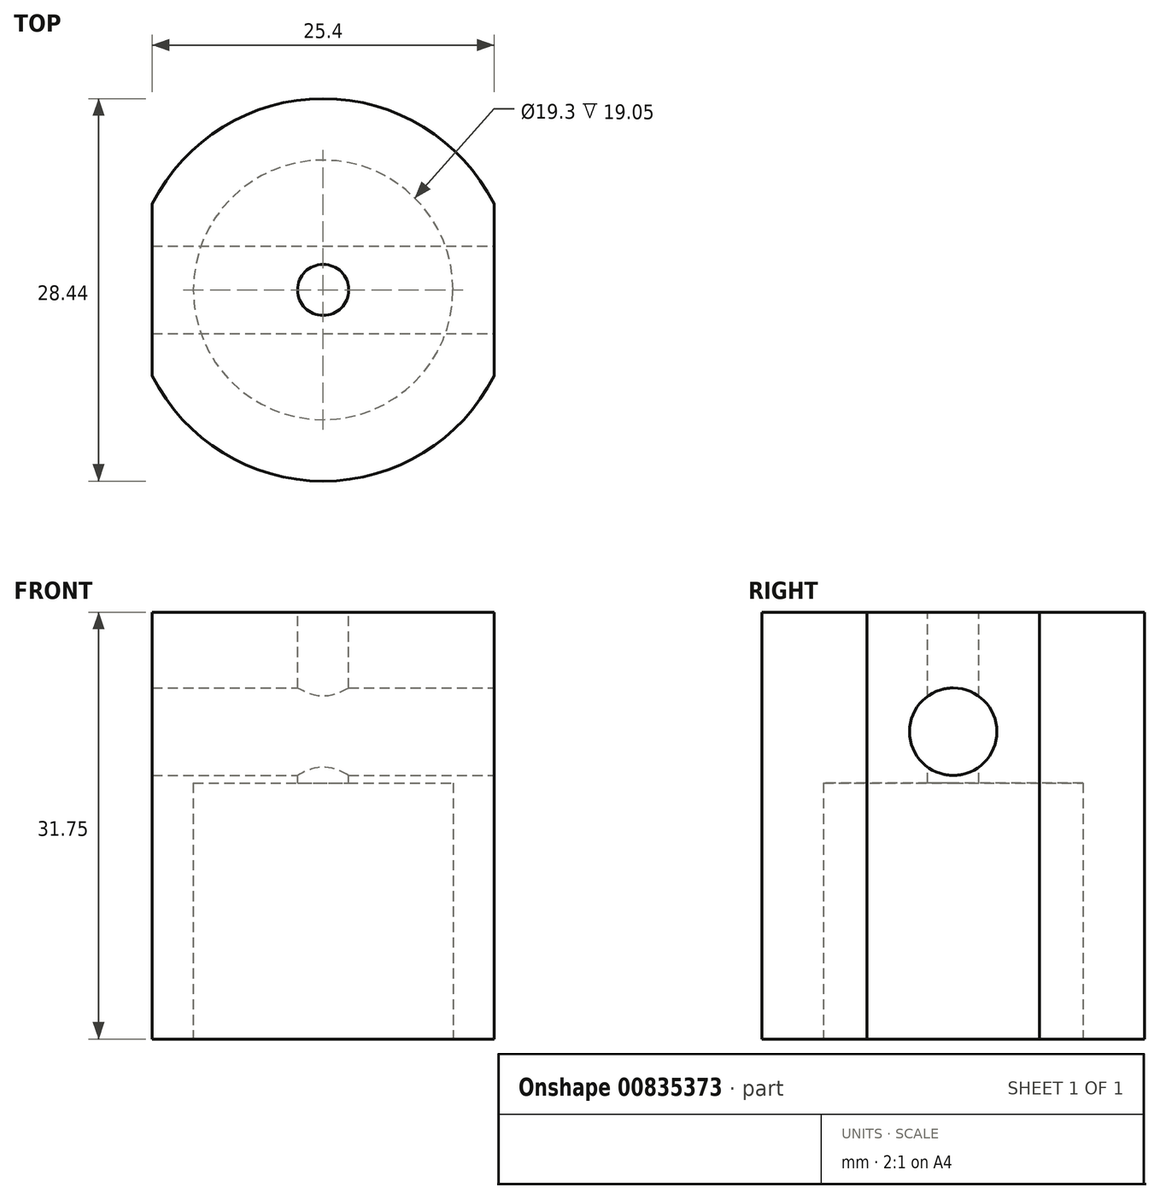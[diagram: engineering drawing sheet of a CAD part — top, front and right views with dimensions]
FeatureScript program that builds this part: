
annotation { "Feature Type Name" : "Feature", "Feature Type Description" : "" }
export const myFeature = defineFeature(function(context is Context, id is Id, definition is map)
    precondition{}
    {
        {
            var Q0;
            Q0=qCreatedBy(makeId("Top.planeOp"),FACE);
            var sketch = newSketch(context, id + "F0", { "sketchPlane" : qUnion([Q0])});
            skCircle(sketch, "E0", {"center": v(0, 0) * mm, "radius": 14.22 * mm});
            skSolve(sketch);
        }
        {
            var Q0;
            Q0 = qSketchRegion(id + "F0", true);
            extrude(context, id + "F1", {"entities" : qUnion([Q0]), "depth" : 31.75 * mm, "offsetDistance" : 25.4 * mm});
        }
        {
            var Q0;
            Q0=makeQuery(id+"F1.opExtrude","CAP_FACE",FACE,{"disambiguationData":[OSD([sQuery(id+"F0.wireOp",EDGE,"E0")])],"isStart":true});
            var sketch = newSketch(context, id + "F2", { "sketchPlane" : qUnion([Q0])});
            skCircle(sketch, "E1", {"center": v(0, 0) * mm, "radius": 9.65 * mm});
            skSolve(sketch);
        }
        {
            var Q0;
            Q0 = qSketchRegion(id + "F2", true);
            extrude(context, id + "F3", {"entities" : qUnion([Q0]), "operationType" : NewBodyOperationType.REMOVE, "oppositeDirection" : true, "depth" : 19.05 * mm, "offsetDistance" : 25.4 * mm});
        }
        {
            var Q0;
            Q0=makeQuery(id+"F1.opExtrude","CAP_FACE",FACE,{"disambiguationData":[OSD([sQuery(id+"F0.wireOp",EDGE,"E0")])],"isStart":false});
            var sketch = newSketch(context, id + "F4", { "sketchPlane" : qUnion([Q0])});
            skPoint(sketch, "E2", {"position": v(0, 0) * mm});
            skSolve(sketch);
        }
        {
            var Q0;
            Q0=sQuery(id+"F4.wireOp",VERTEX,"E2");
            var Q1;
            Q1=makeQuery(id+"F1.opExtrude","SWEPT_BODY",BODY,{"disambiguationData":[OSD([sQuery(id+"F0.wireOp",EDGE,"E0")])]});
            hole(context, id + "F5", {"style" : HoleStyle.SIMPLE, "endStyle" : HoleEndStyle.THROUGH, "standardTappedOrClearance" : lookupTablePath({ "standard" : "ANSI", "engagement" : "75%", "pitch" : "24 tpi", "size" : "#10", "type" : "Tapped" }), "standardBlindInLast" : lookupTablePath({ "standard" : "ANSI", "engagement" : "75%", "pitch" : "24 tpi", "size" : "#10", "type" : "Tapped" }), "holeDiameter" : 3.8 * mm, "majorDiameter" : 4.83 * mm, "showTappedDepth" : true, "tappedDepth" : 6.36 * mm, "tapClearance" : 3, "locations" : qUnion([Q0]), "scope" : qUnion([Q1])});
        }
        {
            var Q0;
            Q0=makeQuery(id+"F1.opExtrude","CAP_FACE",FACE,{"disambiguationData":[OSD([sQuery(id+"F0.wireOp",EDGE,"E0")])],"isStart":false});
            var sketch = newSketch(context, id + "F6", { "sketchPlane" : qUnion([Q0])});
            skArc(sketch, "E3.0", {"start": v(-12.7, 6.4) * mm, "mid": v(-14.22, 0) * mm, "end": v(-12.7, -6.4) * mm});
            skLineSegment(sketch, "E4", {"start": v(-12.7, 6.4) * mm, "end": v(-12.7, -6.4) * mm});
            skLineSegment(sketch, "E5", {"start": v(12.7, 6.4) * mm, "end": v(12.7, -6.4) * mm});
            skLineSegment(sketch, "E6", {"start": v(-12.7, 0) * mm, "end": v(12.7, 0) * mm, "construction": true});
            skArc(sketch, "E7.trimOffspring", {"start": v(12.7, -6.4) * mm, "mid": v(14.22, 0) * mm, "end": v(12.7, 6.4) * mm});
            skSolve(sketch);
        }
        {
            var Q0;
            Q0 = qSketchRegion(id + "F6", true);
            extrude(context, id + "F7", {"entities" : qUnion([Q0]), "operationType" : NewBodyOperationType.REMOVE, "endBound" : BoundingType.UP_TO_NEXT, "oppositeDirection" : true, "depth" : 25.4 * mm, "offsetDistance" : 25.4 * mm});
        }
        {
            var Q0;
            Q0=makeQuery(id+"F7.boolean.opBoolean","COPY",FACE,{"derivedFrom":makeQuery(id+"F7.opExtrude","SWEPT_FACE",FACE,{"disambiguationData":[OSD([sQuery(id+"F6.wireOp",EDGE,"E5")])]})});
            var sketch = newSketch(context, id + "F8", { "sketchPlane" : qUnion([Q0])});
            skCircle(sketch, "E8", {"center": v(0, 22.86) * mm, "radius": 3.25 * mm});
            skSolve(sketch);
        }
        {
            var Q0;
            Q0 = qSketchRegion(id + "F8", true);
            extrude(context, id + "F9", {"entities" : qUnion([Q0]), "operationType" : NewBodyOperationType.REMOVE, "endBound" : BoundingType.THROUGH_ALL, "oppositeDirection" : true, "depth" : 25.4 * mm, "offsetDistance" : 25.4 * mm});
        }
    });
